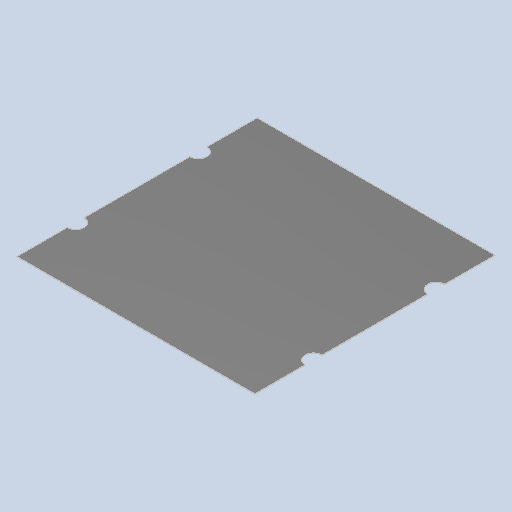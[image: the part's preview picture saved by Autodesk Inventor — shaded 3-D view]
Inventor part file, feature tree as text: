
AUTODESK INVENTOR PART (.ipt)
format: ipt  version: 2023 (Build 270158000, 158)  size: 119,808 bytes
history: native  units: in
note: dims shown in document units (in); Inventor stores cm internally (conversion verified against a paired STEP export)
features: extrude x2, sketch x2
ambient origin geometry x8: Origin, YZ Plane, XZ Plane, XY Plane, X Axis, Y Axis, Z Axis, Center Point
bodies: Solid1 (feature_tree)
feature tree (4):
  extrude  "Extrusion1"  Depth=1.6378in
  extrude  "Extrusion2"  Depth=0.0591in
  sketch  "Sketch1"  dims[d0=1.6535in d1=1.6378in]
  sketch  "Sketch2"  dims[d2=0.0031in d3=0.0in d5=0.0591in d6=0.0in d7=0.0in d8=0.1181in d9=0.4045in]
